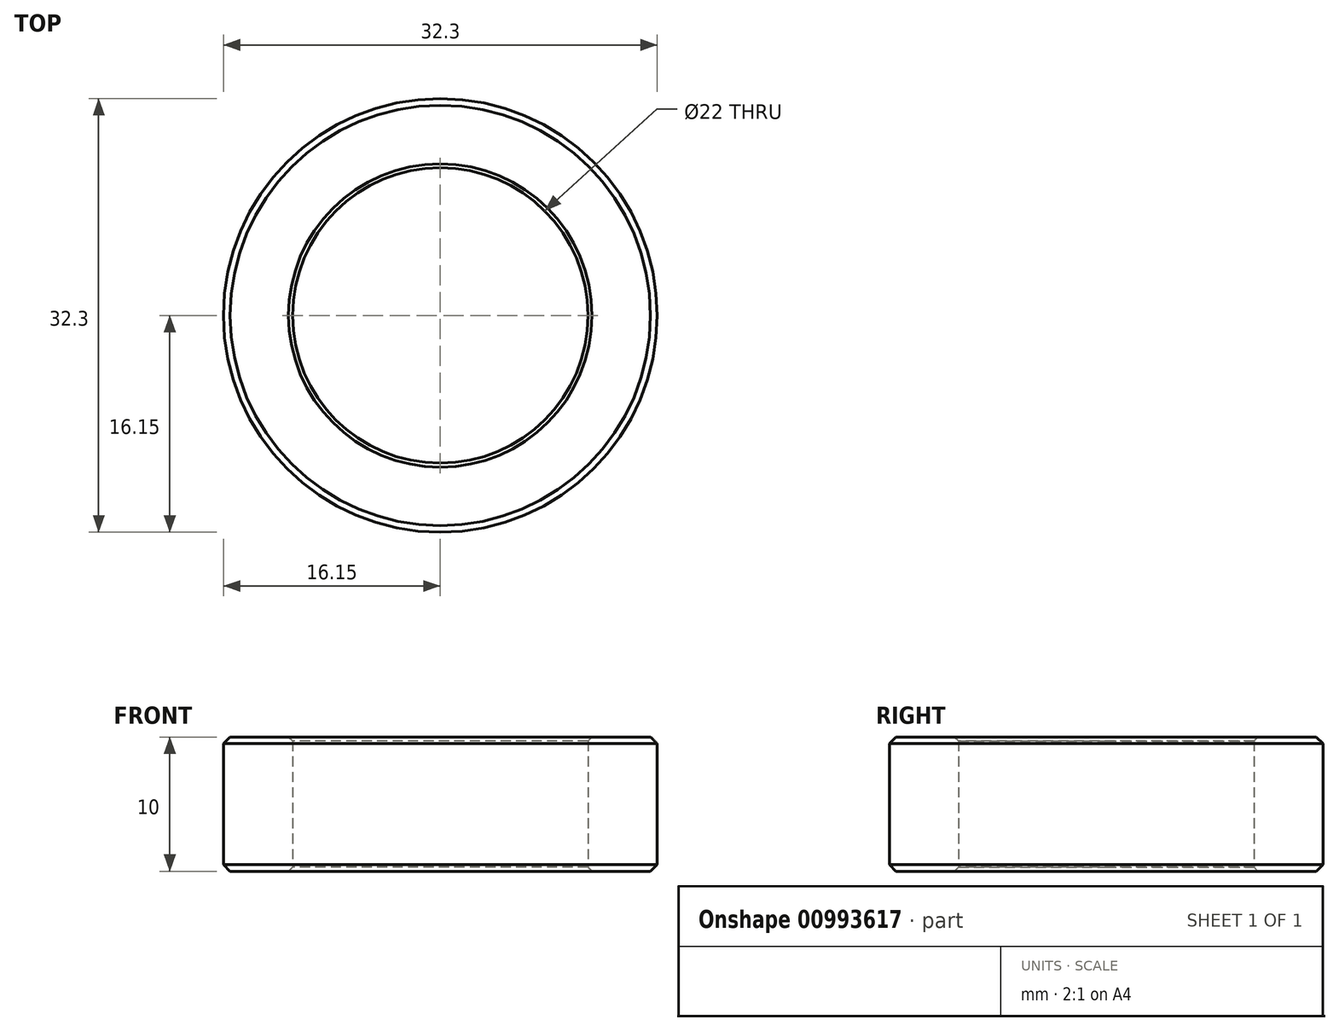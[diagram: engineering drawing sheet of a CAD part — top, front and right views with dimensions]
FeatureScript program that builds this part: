
annotation { "Feature Type Name" : "Feature", "Feature Type Description" : "" }
export const myFeature = defineFeature(function(context is Context, id is Id, definition is map)
    precondition{}
    {
        {
            var Q0;
            Q0=qCreatedBy(makeId("Top.planeOp"),FACE);
            var sketch = newSketch(context, id + "F0", { "sketchPlane" : qUnion([Q0])});
            skCircle(sketch, "E0", {"center": v(0, 0) * mm, "radius": 16.15 * mm});
            skCircle(sketch, "E1", {"center": v(0, 0) * mm, "radius": 11 * mm});
            skSolve(sketch);
        }
        {
            var Q0;
            Q0 = qSketchRegion(id + "F0", true);
            extrude(context, id + "F1", {"entities" : qUnion([Q0]), "depth" : 10 * mm, "offsetDistance" : 25 * mm});
        }
        {
            var Q0;
            Q0=makeQuery(id+"F1.opExtrude","CAP_EDGE",EDGE,{"disambiguationData":[OSD([sQuery(id+"F0.wireOp",EDGE,"E1")])],"isStart":false});
            var Q1;
            Q1=makeQuery(id+"F1.opExtrude","CAP_EDGE",EDGE,{"disambiguationData":[OSD([sQuery(id+"F0.wireOp",EDGE,"E1")])],"isStart":true});
            chamfer(context, id + "F2", {"entities" : qUnion([Q0, Q1]), "width" : 0.3 * mm, "tangentPropagation" : true});
        }
        {
            var Q0;
            Q0=makeQuery(id+"F1.opExtrude","CAP_EDGE",EDGE,{"disambiguationData":[OSD([sQuery(id+"F0.wireOp",EDGE,"E0")])],"isStart":false});
            var Q1;
            Q1=makeQuery(id+"F1.opExtrude","CAP_EDGE",EDGE,{"disambiguationData":[OSD([sQuery(id+"F0.wireOp",EDGE,"E0")])],"isStart":true});
            chamfer(context, id + "F3", {"entities" : qUnion([Q0, Q1]), "width" : 0.5 * mm, "tangentPropagation" : true});
        }
    });
